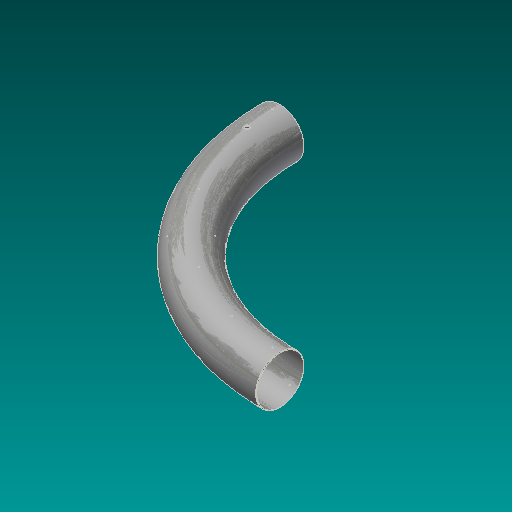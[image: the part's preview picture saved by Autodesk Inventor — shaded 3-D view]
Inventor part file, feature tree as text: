
AUTODESK INVENTOR PART (.ipt)
format: ipt  version: 2017.3 (Build 213257000, 257)  size: 426,496 bytes
history: native  units: in
note: dims shown in document units (in); Inventor stores cm internally (conversion verified against a paired STEP export)
features: plane x9, pattern_circular x7, other x5, hole x3, chamfer x2, sketch x2, revolve x1, split x1, extrude x1
ambient origin geometry x8: Origin, YZ Plane, XZ Plane, XY Plane, X Axis, Y Axis, Z Axis, Center Point
bodies: Solid1 (feature_tree)
feature tree (31):
  revolve  "Revolution1"  [1 undecoded]
  chamfer  "Chamfer3"  Angle=90.0deg  [1 undecoded]
  chamfer  "Chamfer4"  Distance=0.4375in
  plane  "Work Plane1"
  sketch  "Sketch4"  dims[d2=160.0in d3=90.0deg d14=0.4375in d15=0.125in d16=0.2577in d17=0.4375in d18=0.125in d19=0.2577in d20=18.01in d21=160.0in d22=27.2835in d23=4.125in d24=160.0in d25=6.0in d26=0.0148in d27=15.0deg d28=2.5625in d29=0.75in d30=0.375in d31=0.25in d32=0.5635in d33=1.0in d34=0.8108in d35=1.0in d36=0.0in d37=0.891in d38=0.553in d39=0.0246in d40=0.897in d41=0.375in d42=0.25in d43=0.5635in d44=0.91in d45=0.8108in d46=0.891in d47=0.553in d48=0.0246in d49=0.897in d50=0.375in d51=0.25in d52=0.5635in d53=0.91in d54=0.8108in d55=0.0148in d56=-160.0in d57=15.0deg d58=-160.0in d59=1.1811in d60=135.0deg d62=0.7874in d63=180.0deg d65=0.7874in d66=60.0deg d68=0.7874in d69=30.0deg d71=0.0675in d72=0.0675in d73=-160.0in d74=0.2944in d75=-160.0in d76=0.7874in d77=0.2944in d79=0.7874in d80=360.0deg d82=0.7874in d83=0.3827in]
  hole  "Hole1"  [1 undecoded]
  split  "Split1"
  other  "Work Axis3"
  hole  "Hole2"  [1 undecoded]
  hole  "Hole3"  [1 undecoded]
  plane  "Work Plane2"
  other  "Work Axis1"
  other  "Work Axis2"
  pattern_circular  "Circular Pattern1"  [2 undecoded]
  pattern_circular  "Circular Pattern2"  [2 undecoded]
  pattern_circular  "Circular Pattern3"  [2 undecoded]
  pattern_circular  "Circular Pattern4"  [2 undecoded]
  pattern_circular  "Circular Pattern7"  [2 undecoded]
  other  "Work Axis4"
  pattern_circular  "Circular Pattern5"  [2 undecoded]
  pattern_circular  "Circular Pattern6"  [2 undecoded]
  sketch  "Sketch1"  dims[d0=36.0in d1=35.0in]
  other  "Srf1"
  plane  "Work Plane3"
  plane  "Work Plane4"
  plane  "Work Plane5"
  plane  "Work Plane6"
  plane  "Work Plane7"
  plane  "Work Plane8"
  plane  "Work Plane9"
  extrude  "ExtrusionSrf1"  TaperAngle=15.0deg  [1 undecoded]
note: 20 required parameter values undecoded (feature->parameter linkage not recoverable at this tier; creation-order binding heuristic only, values carry confidence <= 0.55)